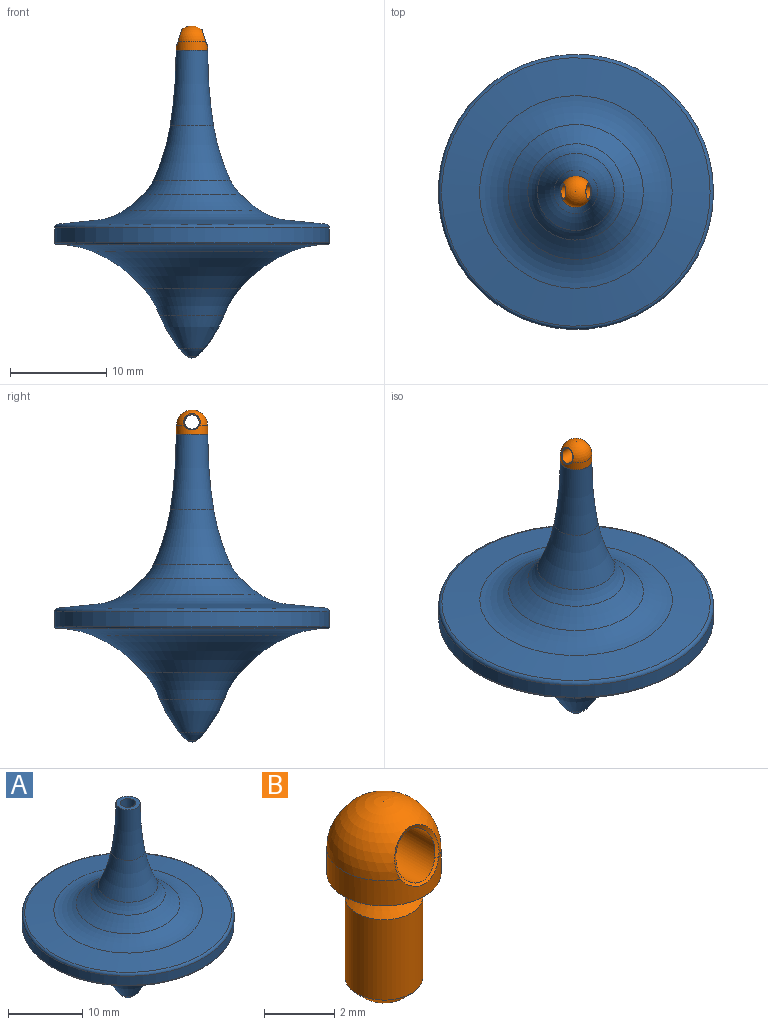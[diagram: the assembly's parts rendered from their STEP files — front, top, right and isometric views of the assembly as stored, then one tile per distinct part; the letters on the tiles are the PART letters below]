
ASSEMBLY  parts=2 mates=1
PART A: 18 faces, bbox 45.9x45.9x35.5 mm
  f0: plane 3.25x3.25mm, normal (0,0,1), area 5mm2, adj f15,f17
  f1: sphere r=0.8mm, area 0.9mm2, adj f2
  f2: revolved ~2.7x2.7mm, area 7mm2, adj f1,f3
  f3: revolved ~6.66x6.66mm, area 60.5mm2, adj f2,f4
  f4: torus R=12.21mm, axis (0,0,1), area 84.2mm2, adj f3,f5
  f5: torus R=15.62mm, axis (0,0,1), area 307.5mm2, adj f4,f6
  f6: torus R=14.09mm, axis (0,0,1), area 300.5mm2, adj f5,f7
  f7: torus R=14.09mm, axis (0,0,1), area 28.1mm2, adj f6,f8
  f8: cylinder r=14.29mm len=28.58mm, axis (0,0,1), area 134.7mm2, adj f7,f9
  f9: torus R=13.89mm, axis (0,0,1), area 51.3mm2, adj f8,f10
  f10: torus R=5.31mm, axis (0,0,1), area 297.9mm2, adj f9,f11
  f11: torus R=10.43mm, axis (0,0,1), area 171mm2, adj f10,f12
  f12: torus R=15.56mm, axis (0,0,1), area 97.8mm2, adj f11,f13
  f13: torus R=8.52mm, axis (0,0,1), area 48.8mm2, adj f12,f14
  f14: torus R=22.99mm, axis (0,0,1), area 111.7mm2, adj f13,f15
  f15: torus R=51.62mm, axis (0,0,1), area 91.2mm2, adj f0,f14
  f16: cone r=0mm half-angle=59deg, axis (0,0,1), area 3.9mm2, adj f17
  f17: cylinder r=1.03mm len=6mm, axis (0,0,1), area 38.6mm2, adj f0,f16
PART B: 13 faces, bbox 3.3x3.3x6.5 mm
  f0: plane 1.5x1.5mm, normal (0,0,-1), area 1.8mm2, adj f1
  f1: cone r=1.1mm half-angle=45deg, axis (0,0,1), area 2.9mm2, adj f0,f2
  f2: cylinder r=1.1mm len=2.8mm, axis (0,0,-1), area 19.4mm2, adj f1,f3
  f3: cone r=0.75mm half-angle=45deg, axis (0,0,-1), area 2.9mm2, adj f2,f4
  f4: cylinder r=0.75mm len=1.5mm, axis (0,0,-1), area 2.4mm2, adj f3,f5
  f5: plane 3.25x3.25mm, normal (0,0,-1), area 6.5mm2, adj f4,f6
  f6: cylinder r=1.62mm len=3.25mm, axis (0,0,-1), area 7.9mm2, adj f5,f7,f10,f12
  f7: sphere r=1.62mm, area 12.4mm2, adj f6,f9,f11
  f8: cylinder r=0.75mm len=2.75mm, axis (0,-1,0), area 12.9mm2, adj f9,f10,f11,f12
  f9: bspline ~1.79x1.25mm, area 0.4mm2, adj f7,f8,f10
  f10: bspline ~1.52x0.48mm, area 0.2mm2, adj f6,f8,f9
  f11: bspline ~1.79x1.25mm, area 0.4mm2, adj f7,f8,f12
  f12: bspline ~1.52x0.48mm, area 0.2mm2, adj f6,f8,f11
PLACE A t=(0,0,-19.08)mm
PLACE B rot(axis=(0,0,1),90deg) t=(0,0,-19.08)mm
MATE cylindrical B.f2 <-> A.f15  axis (0,0,-1) through (0,0,0)mm
